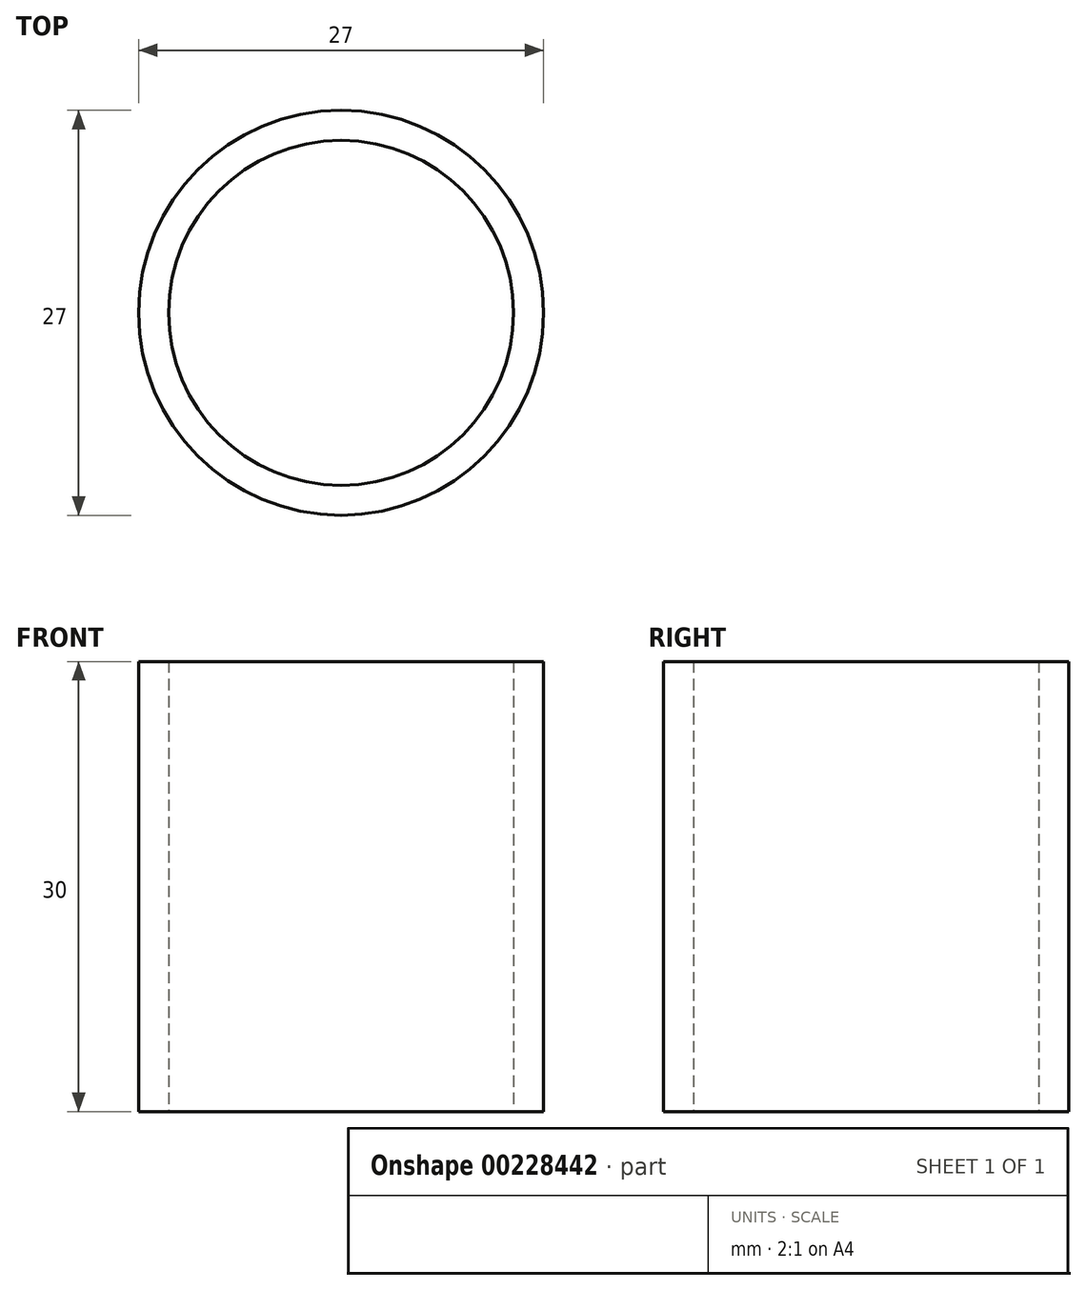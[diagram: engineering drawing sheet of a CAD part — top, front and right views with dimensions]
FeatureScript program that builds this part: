
annotation { "Feature Type Name" : "Feature", "Feature Type Description" : "" }
export const myFeature = defineFeature(function(context is Context, id is Id, definition is map)
    precondition{}
    {
        {
            var Q0;
            Q0=qCreatedBy(makeId("Top.planeOp"),FACE);
            var sketch = newSketch(context, id + "F0", { "sketchPlane" : qUnion([Q0])});
            skCircle(sketch, "E0", {"center": v(0, 0) * mm, "radius": 11.5 * mm});
            skCircle(sketch, "E1", {"center": v(0, 0) * mm, "radius": 13.5 * mm});
            skSolve(sketch);
        }
        {
            var Q0;
            Q0=makeQuery(id+"F0.imprint","IMPRINT",FACE,{"disambiguationData":[TD([[makeQuery(id+"F0.imprint","IMPRINT",EDGE,{"derivedFrom":sQuery(id+"F0.wireOp",EDGE,"E0")}),-1.0]])]});
            extrude(context, id + "F1", {"entities" : qUnion([Q0]), "depth" : 30 * mm});
        }
    });
